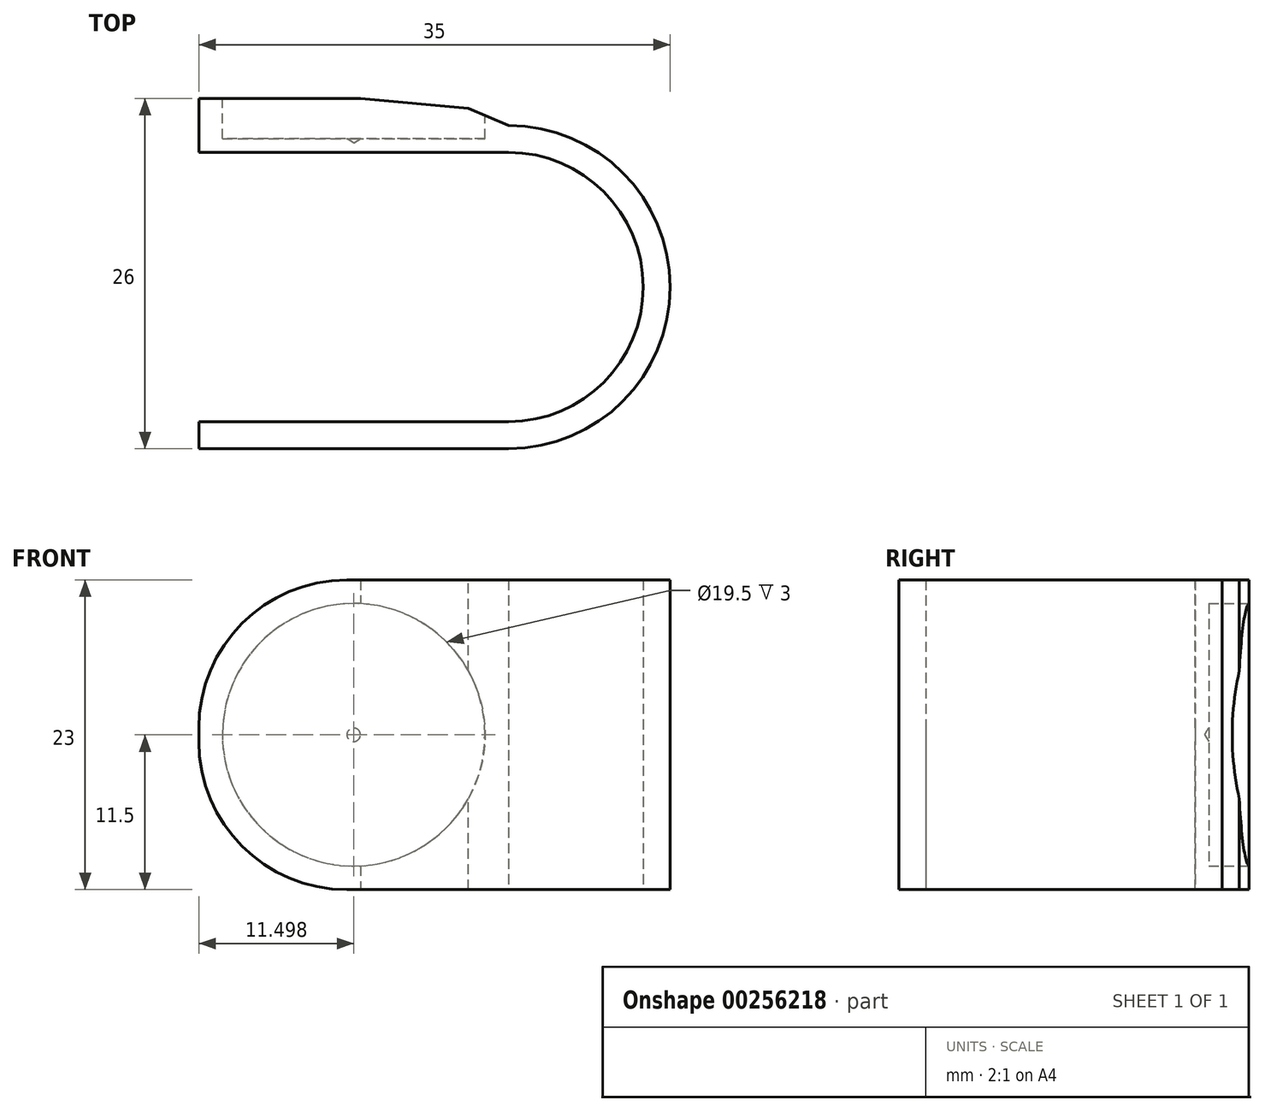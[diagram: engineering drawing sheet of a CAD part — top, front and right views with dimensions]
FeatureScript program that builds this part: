
annotation { "Feature Type Name" : "Feature", "Feature Type Description" : "" }
export const myFeature = defineFeature(function(context is Context, id is Id, definition is map)
    precondition{}
    {
        {
            var Q0;
            Q0=qCreatedBy(makeId("Top.planeOp"),FACE);
            var sketch = newSketch(context, id + "F0", { "sketchPlane" : qUnion([Q0])});
            skLineSegment(sketch, "E0", {"start": v(-8.38, 0) * mm, "end": v(14.62, 0) * mm});
            skLineSegment(sketch, "E1", {"start": v(14.62, 0) * mm, "end": v(14.62, -20) * mm});
            skArc(sketch, "E2", {"start": v(14.62, -20) * mm, "mid": v(24.62, -10) * mm, "end": v(14.62, 0) * mm});
            skLineSegment(sketch, "E3", {"start": v(14.62, -20) * mm, "end": v(-8.38, -20) * mm});
            skLineSegment(sketch, "E4.0", {"start": v(14.62, -22) * mm, "end": v(-8.38, -22) * mm});
            skArc(sketch, "E4.1", {"start": v(14.62, -22) * mm, "mid": v(26.62, -10) * mm, "end": v(14.62, 2) * mm});
            skLineSegment(sketch, "E4.2", {"start": v(-8.38, 2) * mm, "end": v(14.62, 2) * mm});
            skLineSegment(sketch, "E5", {"start": v(-8.38, 2) * mm, "end": v(-8.38, 0) * mm});
            skLineSegment(sketch, "E6", {"start": v(-8.38, -20) * mm, "end": v(-8.38, -22) * mm});
            skLineSegment(sketch, "E7", {"start": v(-8.38, 2) * mm, "end": v(-8.38, 4) * mm});
            skLineSegment(sketch, "E8", {"start": v(-8.38, 4) * mm, "end": v(14.62, 4) * mm});
            skLineSegment(sketch, "E9", {"start": v(14.62, 4) * mm, "end": v(14.62, 2) * mm});
            skSolve(sketch);
        }
        {
            var Q0;
            Q0=makeQuery(id+"F0.imprint","IMPRINT",FACE,{"disambiguationData":[TD([[makeQuery(id+"F0.imprint","IMPRINT",EDGE,{"derivedFrom":sQuery(id+"F0.wireOp",EDGE,"E0")}),1.0]])]});
            var Q1;
            Q1=makeQuery(id+"F0.imprint","IMPRINT",FACE,{"disambiguationData":[TD([[makeQuery(id+"F0.imprint","IMPRINT",EDGE,{"derivedFrom":sQuery(id+"F0.wireOp",EDGE,"E4.2")}),1.0]])]});
            extrude(context, id + "F1", {"entities" : qUnion([Q0, Q1]), "depth" : 23 * mm});
        }
        {
            var Q0;
            Q0=makeQuery(id+"F1.opExtrude","SWEPT_FACE",FACE,{"disambiguationData":[OSD([sQuery(id+"F0.wireOp",EDGE,"E8")])]});
            var sketch = newSketch(context, id + "F2", { "sketchPlane" : qUnion([Q0])});
            skLineSegment(sketch, "E10", {"start": v(-14.62, 23) * mm, "end": v(8.38, 0) * mm});
            skLineSegment(sketch, "E11", {"start": v(8.38, 23) * mm, "end": v(-14.62, 0) * mm});
            skPoint(sketch, "E12", {"position": v(-3.12, 11.5) * mm});
            skSolve(sketch);
        }
        {
            var Q0;
            Q0=sQuery(id+"F2.wireOp",VERTEX,"E12");
            var Q1;
            Q1=makeQuery(id+"F1.opExtrude","SWEPT_BODY",BODY,{"disambiguationData":[OSD([sQuery(id+"F0.wireOp",EDGE,"E0"),sQuery(id+"F0.wireOp",EDGE,"E2"),sQuery(id+"F0.wireOp",EDGE,"E3"),sQuery(id+"F0.wireOp",EDGE,"E4.0"),sQuery(id+"F0.wireOp",EDGE,"E4.1"),sQuery(id+"F0.wireOp",EDGE,"E5"),sQuery(id+"F0.wireOp",EDGE,"E6"),sQuery(id+"F0.wireOp",EDGE,"E7"),sQuery(id+"F0.wireOp",EDGE,"E8"),sQuery(id+"F0.wireOp",EDGE,"E9")])]});
            hole(context, id + "F3", {"style" : HoleStyle.C_BORE, "endStyle" : HoleEndStyle.BLIND, "holeDiameter" : 1 * mm, "cBoreDiameter" : 19.5 * mm, "cBoreDepth" : 3 * mm, "holeDepth" : 3 * mm, "tappedDepth" : 12 * mm, "tapClearance" : 3, "locations" : qUnion([Q0]), "scope" : qUnion([Q1])});
        }
        {
            var Q0;
            Q0=makeQuery(id+"F1.opExtrude","CAP_EDGE",EDGE,{"disambiguationData":[OSD([sQuery(id+"F0.wireOp",EDGE,"E5"),sQuery(id+"F0.wireOp",EDGE,"E7")])],"isStart":false});
            var Q1;
            Q1=makeQuery(id+"F1.opExtrude","CAP_EDGE",EDGE,{"disambiguationData":[OSD([sQuery(id+"F0.wireOp",EDGE,"E5"),sQuery(id+"F0.wireOp",EDGE,"E7")])],"isStart":true});
            var Q2;
            Q2=makeQuery(id+"F1.opExtrude","CAP_EDGE",EDGE,{"disambiguationData":[OSD([sQuery(id+"F0.wireOp",EDGE,"E6")])],"isStart":true});
            var Q3;
            Q3=makeQuery(id+"F1.opExtrude","CAP_EDGE",EDGE,{"disambiguationData":[OSD([sQuery(id+"F0.wireOp",EDGE,"E6")])],"isStart":false});
            fillet(context, id + "F4", {"entities" : qUnion([Q0, Q1, Q2, Q3]), "radius" : 11 * mm, "tangentPropagation" : true, "allowEdgeOverflow" : false});
        }
        {
            var Q0;
            Q0=makeQuery(id+"F1.opExtrude","SWEPT_EDGE",EDGE,{"disambiguationData":[OSD([sQuery(id+"F0.wireOp",EDGE,"E8"),sQuery(id+"F0.wireOp",EDGE,"E9")])]});
            chamfer(context, id + "F5", {"entities" : qUnion([Q0]), "chamferType" : ChamferType.TWO_OFFSETS, "width1" : 11 * mm, "oppositeDirection" : false, "width2" : 1 * mm, "tangentPropagation" : true});
        }
        {
            var Q0;
            {var subQ0=sQuery(id+"F0.wireOp",EDGE,"E9");Q0=makeQuery(id+"F5.opChamfer","BLEND_EDGE",EDGE,{"blendedFrom":[makeQuery(id+"F1.opExtrude","SWEPT_EDGE",EDGE,{"disambiguationData":[OSD([sQuery(id+"F0.wireOp",EDGE,"E8"),subQ0])]}),makeQuery(id+"F1.opExtrude","SWEPT_FACE",FACE,{"disambiguationData":[OSD([subQ0])]})],"blendedInto":[makeQuery(id+"F1.opExtrude","SWEPT_FACE",FACE,{"disambiguationData":[OSD([subQ0])]})]});}
            chamfer(context, id + "F6", {"entities" : qUnion([Q0]), "chamferType" : ChamferType.TWO_OFFSETS, "width1" : 1 * mm, "oppositeDirection" : false, "width2" : 3 * mm, "tangentPropagation" : true});
        }
    });
